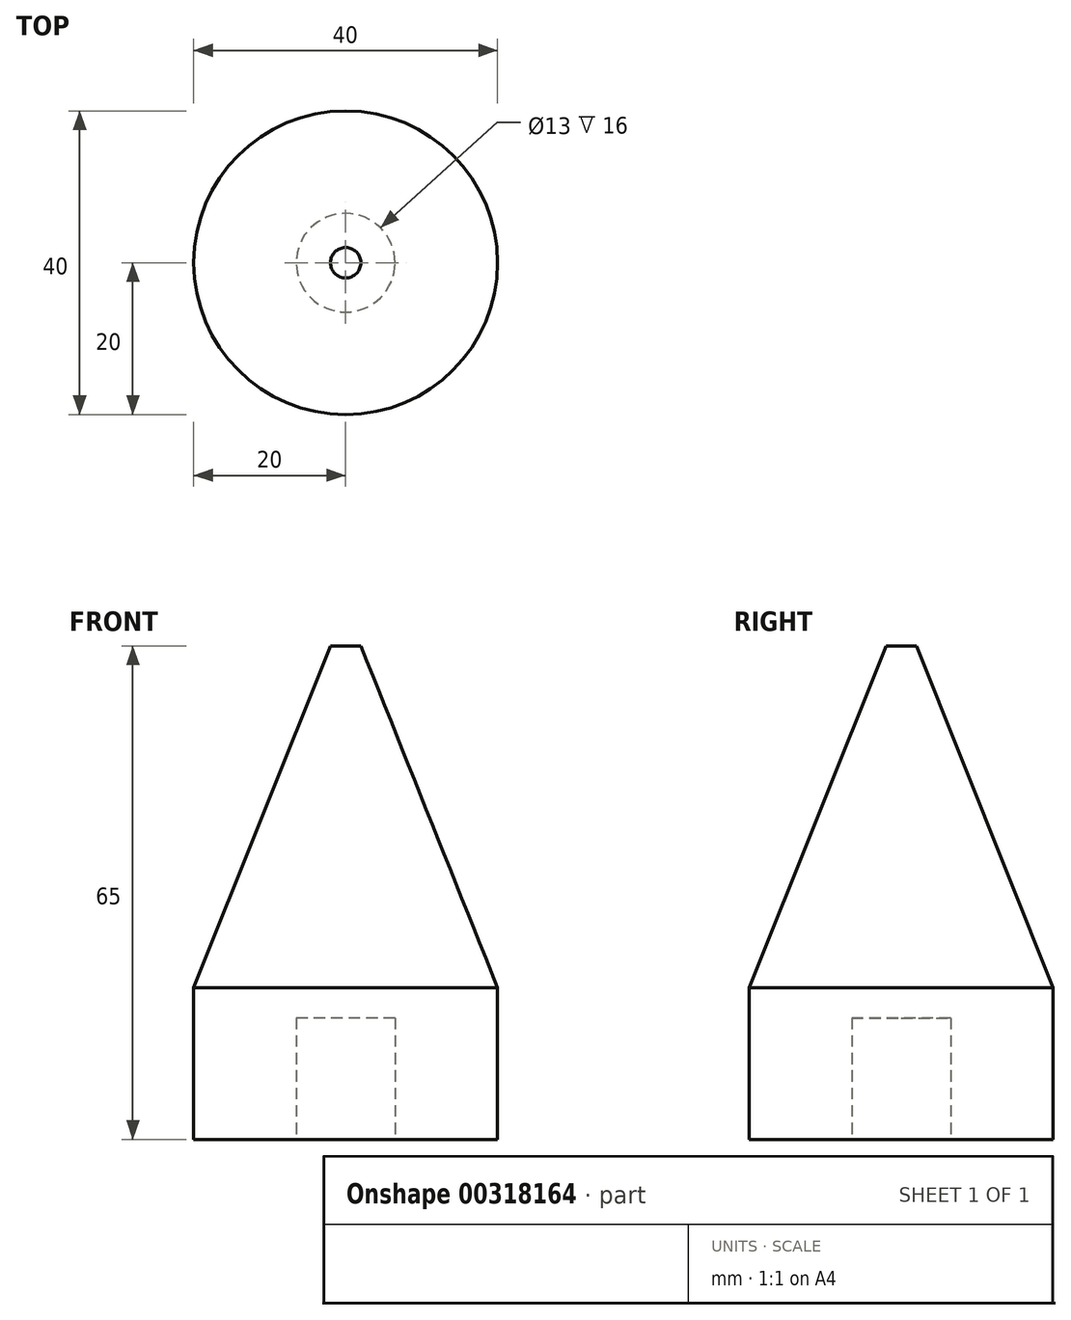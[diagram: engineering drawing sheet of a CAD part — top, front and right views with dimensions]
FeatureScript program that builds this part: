
annotation { "Feature Type Name" : "Feature", "Feature Type Description" : "" }
export const myFeature = defineFeature(function(context is Context, id is Id, definition is map)
    precondition{}
    {
        {
            var Q0;
            Q0=qCreatedBy(makeId("Top.planeOp"),FACE);
            var sketch = newSketch(context, id + "F0", { "sketchPlane" : qUnion([Q0])});
            skCircle(sketch, "E0", {"center": v(0, 0) * mm, "radius": 20 * mm});
            skCircle(sketch, "E1", {"center": v(0, 0) * mm, "radius": 1.5 * mm});
            skCircle(sketch, "E2", {"center": v(0, 0) * mm, "radius": 6.5 * mm});
            skSolve(sketch);
        }
        {
            var Q0;
            Q0=makeQuery(id+"F0.imprint","IMPRINT",FACE,{"disambiguationData":[TD([[makeQuery(id+"F0.imprint","IMPRINT",EDGE,{"derivedFrom":sQuery(id+"F0.wireOp",EDGE,"E0")}),1.0]])]});
            var Q1;
            Q1=makeQuery(id+"F0.imprint","IMPRINT",FACE,{"disambiguationData":[TD([[makeQuery(id+"F0.imprint","IMPRINT",EDGE,{"derivedFrom":sQuery(id+"F0.wireOp",EDGE,"E1")}),-1.0]])]});
            var Q2;
            Q2=makeQuery(id+"F0.imprint","IMPRINT",FACE,{"disambiguationData":[TD([[makeQuery(id+"F0.imprint","IMPRINT",EDGE,{"derivedFrom":sQuery(id+"F0.wireOp",EDGE,"E1")}),1.0]])]});
            extrude(context, id + "F1", {"entities" : qUnion([Q0, Q1, Q2]), "offsetDistance" : 25 * mm, "depth" : 65 * mm});
        }
        {
            var Q0;
            Q0=makeQuery(id+"F1.opExtrude","CAP_EDGE",EDGE,{"disambiguationData":[OSD([sQuery(id+"F0.wireOp",EDGE,"E0")])],"isStart":false});
            chamfer(context, id + "F2", {"entities" : qUnion([Q0]), "chamferType" : ChamferType.TWO_OFFSETS, "width1" : 18 * mm, "oppositeDirection" : false, "width2" : 45 * mm, "tangentPropagation" : true});
        }
        {
            var Q0;
            Q0=makeQuery(id+"F0.imprint","IMPRINT",FACE,{"disambiguationData":[TD([[makeQuery(id+"F0.imprint","IMPRINT",EDGE,{"derivedFrom":sQuery(id+"F0.wireOp",EDGE,"E1")}),-1.0]])]});
            var Q1;
            Q1=makeQuery(id+"F0.imprint","IMPRINT",FACE,{"disambiguationData":[TD([[makeQuery(id+"F0.imprint","IMPRINT",EDGE,{"derivedFrom":sQuery(id+"F0.wireOp",EDGE,"E1")}),1.0]])]});
            extrude(context, id + "F3", {"entities" : qUnion([Q0, Q1]), "operationType" : NewBodyOperationType.REMOVE, "depth" : 16 * mm});
        }
    });
